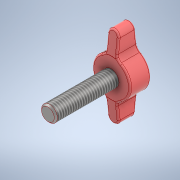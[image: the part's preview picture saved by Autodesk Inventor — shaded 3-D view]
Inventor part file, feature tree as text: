
AUTODESK INVENTOR PART (.ipt)
format: ipt  version: 2020 (Build 240168000, 168)  size: 413,184 bytes
history: native  units: mm
features: sketch x4, extrude x3, fillet x2, revolve x1, mirror x1, chamfer x1, thread x1, projected_geometry x1
ambient origin geometry x8: Origin, YZ Plane, XZ Plane, XY Plane, X Axis, Y Axis, Z Axis, Center Point
bodies: Solid1 (feature_tree)
feature tree (14):
  extrude  "Extrusion1"  Depth=6.6mm TaperAngle=0.0deg
  extrude  "Extrusion2"  Depth=26.0mm
  revolve  "Revolution1"  [1 undecoded]
  mirror  "Mirror1"
  fillet  "Fillet1"  Radius=2.5mm
  fillet  "Fillet2"  [1 undecoded]
  extrude  "Extrusion3"  Depth=0.5mm
  chamfer  "Chamfer1"  Distance=5.0mm
  thread  "Thread1"  [1 undecoded]
  sketch  "Sketch1"  dims[d0=12.0mm d1=6.6mm d2=0.0mm]
  sketch  "Sketch2"  dims[d3=3.5mm d4=26.0mm]
  sketch  "Sketch3"  dims[d5=6.6mm d6=0.0mm d7=12.0mm d8=2.5mm d9=90.0deg]
  sketch  "Sketch4"  dims[d10=2.0mm d11=0.5mm d12=5.0mm d13=20.0mm d14=0.0mm d15=0.5mm d16=6.875mm d17=45.0deg d18=19.5mm d19=0.0mm]
  projected_geometry  "Project Cut Edges1"
note: 3 required parameter values undecoded (feature->parameter linkage not recoverable at this tier; creation-order binding heuristic only, values carry confidence <= 0.55)